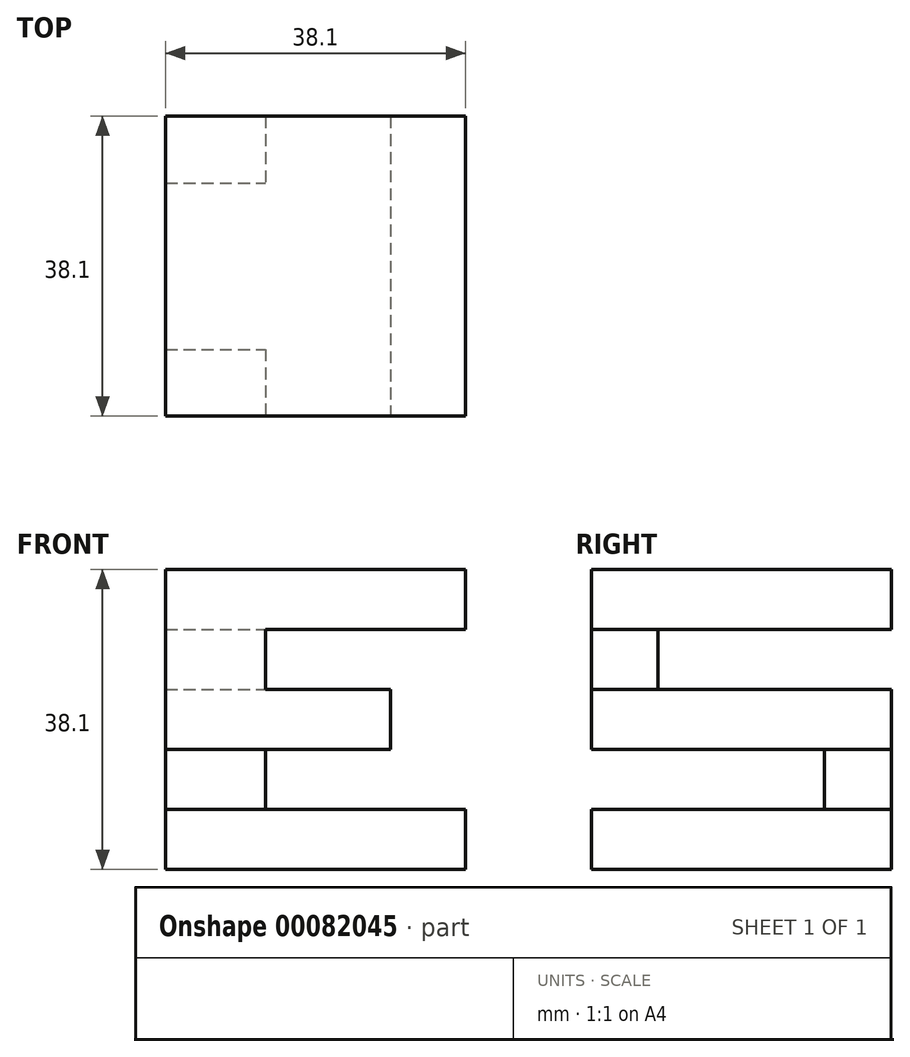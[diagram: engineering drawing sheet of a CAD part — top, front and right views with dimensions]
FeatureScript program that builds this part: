
annotation { "Feature Type Name" : "Feature", "Feature Type Description" : "" }
export const myFeature = defineFeature(function(context is Context, id is Id, definition is map)
    precondition{}
    {
        {
            var Q0;
            Q0=qCreatedBy(makeId("Front.planeOp"),FACE);
            var sketch = newSketch(context, id + "F0", { "sketchPlane" : qUnion([Q0])});
            skLineSegment(sketch, "E0", {"start": v(0, 0) * mm, "end": v(0, 38.1) * mm});
            skLineSegment(sketch, "E1", {"start": v(0, 38.1) * mm, "end": v(38.1, 38.1) * mm});
            skLineSegment(sketch, "E2", {"start": v(38.1, 38.1) * mm, "end": v(38.1, 0) * mm});
            skLineSegment(sketch, "E3", {"start": v(38.1, 0) * mm, "end": v(0, 0) * mm});
            skSolve(sketch);
        }
        {
            var Q0;
            Q0=makeQuery(id+"F0.imprint","IMPRINT",FACE,{"disambiguationData":[TD([[makeQuery(id+"F0.imprint","IMPRINT",EDGE,{"derivedFrom":sQuery(id+"F0.wireOp",EDGE,"E0")}),-1.0]])]});
            extrude(context, id + "F1", {"entities" : qUnion([Q0]), "depth" : 38.1 * mm});
        }
        {
            var Q0;
            Q0=qCreatedBy(makeId("Front.planeOp"),FACE);
            cPlane(context, id + "F2", {"entities" : qUnion([Q0]), "cplaneType" : CPlaneType.OFFSET, "offset" : 38.1 * mm, "width" : 152.4 * mm, "height" : 152.4 * mm});
        }
        {
            var Q0;
            Q0=qCreatedBy(makeId("Right.planeOp"),FACE);
            cPlane(context, id + "F3", {"entities" : qUnion([Q0]), "cplaneType" : CPlaneType.OFFSET, "offset" : 38.1 * mm, "width" : 152.4 * mm, "height" : 152.4 * mm});
        }
        {
            var Q0;
            Q0=qCreatedBy(makeId("Top.planeOp"),FACE);
            cPlane(context, id + "F4", {"entities" : qUnion([Q0]), "cplaneType" : CPlaneType.OFFSET, "offset" : 38.1 * mm, "width" : 152.4 * mm, "height" : 152.4 * mm});
        }
        {
            var Q0;
            Q0=qCreatedBy(id+"F3.planeOp",FACE);
            var sketch = newSketch(context, id + "F5", { "sketchPlane" : qUnion([Q0])});
            skLineSegment(sketch, "E4", {"start": v(0, 30.48) * mm, "end": v(-29.64, 30.48) * mm});
            skLineSegment(sketch, "E5", {"start": v(-29.64, 30.48) * mm, "end": v(-29.64, 22.86) * mm});
            skLineSegment(sketch, "E6", {"start": v(-29.64, 22.86) * mm, "end": v(0, 22.86) * mm});
            skLineSegment(sketch, "E7", {"start": v(0, 22.86) * mm, "end": v(0, 30.48) * mm});
            skLineSegment(sketch, "E8", {"start": v(-38.16, 15.24) * mm, "end": v(-8.52, 15.24) * mm});
            skLineSegment(sketch, "E9", {"start": v(-8.52, 15.24) * mm, "end": v(-8.52, 7.62) * mm});
            skLineSegment(sketch, "E10", {"start": v(-8.52, 7.62) * mm, "end": v(-38.5, 7.62) * mm});
            skLineSegment(sketch, "E11", {"start": v(-38.5, 7.62) * mm, "end": v(-38.16, 15.24) * mm});
            skSolve(sketch);
        }
        {
            var Q0;
            Q0=makeQuery(id+"F5.imprint","IMPRINT",FACE,{"disambiguationData":[TD([[makeQuery(id+"F5.imprint","IMPRINT",EDGE,{"derivedFrom":sQuery(id+"F5.wireOp",EDGE,"E4")}),1.0]])]});
            var Q1;
            Q1=makeQuery(id+"F5.imprint","IMPRINT",FACE,{"disambiguationData":[TD([[makeQuery(id+"F5.imprint","IMPRINT",EDGE,{"derivedFrom":sQuery(id+"F5.wireOp",EDGE,"E8")}),-1.0]])]});
            extrude(context, id + "F6", {"entities" : qUnion([Q0, Q1]), "operationType" : NewBodyOperationType.REMOVE, "oppositeDirection" : true, "depth" : 38.1 * mm});
        }
        {
            var Q0;
            Q0=qCreatedBy(id+"F2.planeOp",FACE);
            var sketch = newSketch(context, id + "F7", { "sketchPlane" : qUnion([Q0])});
            skLineSegment(sketch, "E12", {"start": v(0, 38.1) * mm, "end": v(0, 0) * mm});
            skLineSegment(sketch, "E13", {"start": v(0, 0) * mm, "end": v(38.1, 0) * mm});
            skLineSegment(sketch, "E14", {"start": v(38.1, 0) * mm, "end": v(38.1, 38.1) * mm});
            skLineSegment(sketch, "E15", {"start": v(38.1, 38.1) * mm, "end": v(0, 38.1) * mm});
            skLineSegment(sketch, "E16", {"start": v(38.1, 30.48) * mm, "end": v(12.7, 30.48) * mm});
            skLineSegment(sketch, "E17", {"start": v(12.7, 30.48) * mm, "end": v(12.7, 22.86) * mm});
            skLineSegment(sketch, "E18", {"start": v(12.7, 22.86) * mm, "end": v(28.58, 22.86) * mm});
            skLineSegment(sketch, "E19", {"start": v(28.58, 22.86) * mm, "end": v(28.58, 15.24) * mm});
            skLineSegment(sketch, "E20", {"start": v(28.58, 15.24) * mm, "end": v(12.7, 15.24) * mm});
            skLineSegment(sketch, "E21", {"start": v(12.7, 15.24) * mm, "end": v(12.7, 7.62) * mm});
            skLineSegment(sketch, "E22", {"start": v(12.7, 7.62) * mm, "end": v(38.1, 7.62) * mm});
            skSolve(sketch);
        }
        {
            var Q0;
            {var subQ0=sQuery(id+"F7.wireOp",EDGE,"E16");Q0=makeQuery(id+"F7.imprint","IMPRINT",FACE,{"disambiguationData":[TD([[makeQuery(id+"F7.imprint","IMPRINT",EDGE,{"derivedFrom":subQ0}),1.0]])]});}
            extrude(context, id + "F8", {"entities" : qUnion([Q0]), "operationType" : NewBodyOperationType.REMOVE, "oppositeDirection" : true, "depth" : 38.1 * mm});
        }
    });
